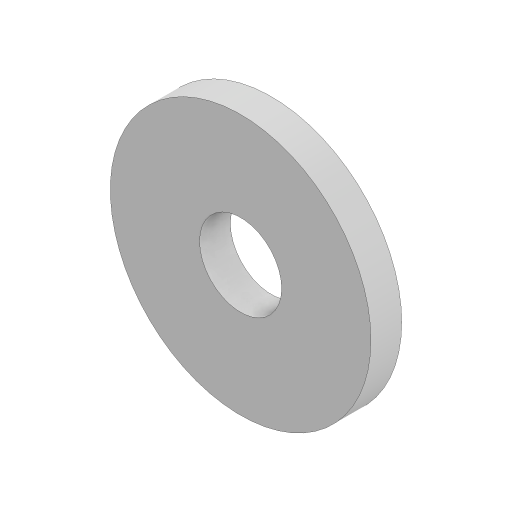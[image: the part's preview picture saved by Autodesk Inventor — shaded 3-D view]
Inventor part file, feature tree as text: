
AUTODESK INVENTOR PART (.ipt)
format: ipt  version: 2023 (Build 270158000, 158)  size: 93,184 bytes
history: native  units: mm
features: extrude x1, sketch x1
ambient origin geometry x8: Origin, YZ Plane, XZ Plane, XY Plane, X Axis, Y Axis, Z Axis, Center Point
bodies: Solid1 (feature_tree)
feature tree (2):
  extrude  "Extrusion1"  Depth=3.0mm
  sketch  "Sketch1"  dims[d0=25.4mm d1=8.0mm d2=3.0mm d3=0.0mm]
